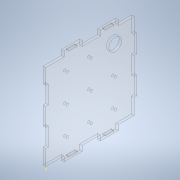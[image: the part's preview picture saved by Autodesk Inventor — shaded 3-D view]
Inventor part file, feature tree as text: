
AUTODESK INVENTOR PART (.ipt)
format: ipt  version: 2021 (Build 250183000, 183)  size: 198,656 bytes
history: native  units: mm
features: sketch x11, hole x9, extrude x1
ambient origin geometry x8: Origin, YZ Plane, XZ Plane, XY Plane, X Axis, Y Axis, Z Axis, Center Point
bodies: Solid1 (feature_tree)
feature tree (21):
  extrude  "Extrusion1"  Depth=3.0mm
  hole  "Hole2"  [1 undecoded]
  hole  "Hole3"  [1 undecoded]
  hole  "Hole4"  [1 undecoded]
  hole  "Hole5"  [1 undecoded]
  hole  "Hole6"  [1 undecoded]
  hole  "Hole7"  [1 undecoded]
  hole  "Hole8"  [1 undecoded]
  hole  "Hole9"  [1 undecoded]
  sketch  "Sketch11"  dims[d87=15.0mm d88=6.0mm d89=4.0mm d90=2.0mm d91=90.0deg d92=8.0mm d93=20.594885mm d94=1.0mm]
  hole  "Hole10"  [1 undecoded]
  sketch  "Sketch1"  dims[d4=3.0mm d5=0.0mm d22=3.0mm]
  sketch  "Sketch3"  dims[d23=3.0mm d24=6.0mm d25=4.0mm d26=2.0mm d27=90.0deg d28=8.0mm d29=20.594885mm d30=3.0mm]
  sketch  "Sketch4"  dims[d31=3.0mm d32=6.0mm d33=4.0mm d34=2.0mm d35=90.0deg d36=8.0mm d37=20.594885mm d38=3.0mm]
  sketch  "Sketch5"  dims[d39=3.0mm d40=6.0mm d41=4.0mm d42=2.0mm d43=90.0deg d44=8.0mm d45=20.594885mm d46=3.0mm]
  sketch  "Sketch6"  dims[d47=3.0mm d48=6.0mm d49=4.0mm d50=2.0mm d51=90.0deg d52=8.0mm d53=20.594885mm d54=3.0mm]
  sketch  "Sketch7"  dims[d55=3.0mm d56=6.0mm d57=4.0mm d58=2.0mm d59=90.0deg d60=8.0mm d61=20.594885mm d62=3.0mm]
  sketch  "Sketch8"  dims[d63=3.0mm d64=6.0mm d65=4.0mm d66=2.0mm d67=90.0deg d68=8.0mm d69=20.594885mm d70=3.0mm]
  sketch  "Sketch9"  dims[d71=3.0mm d72=6.0mm d73=4.0mm d74=2.0mm d75=90.0deg d76=8.0mm d77=20.594885mm d78=3.0mm]
  sketch  "Sketch10"  dims[d79=3.0mm d80=6.0mm d81=4.0mm d82=2.0mm d83=90.0deg d84=8.0mm d85=20.594885mm d86=3.0mm]
  sketch  "Sketch12"  dims[d95=10.0mm d96=10.0mm d97=1.0mm d98=10.0mm d99=1.0mm d100=10.0mm]
note: 9 required parameter values undecoded (feature->parameter linkage not recoverable at this tier; creation-order binding heuristic only, values carry confidence <= 0.55)
